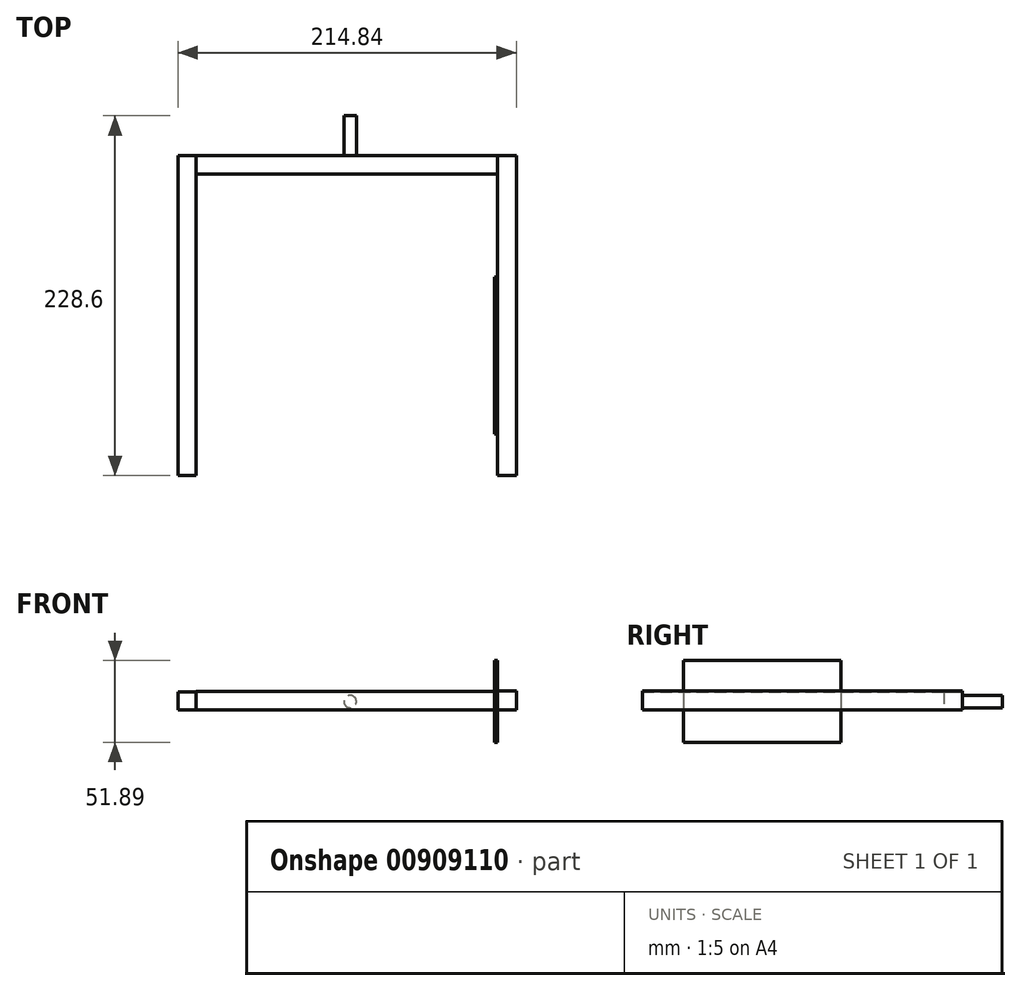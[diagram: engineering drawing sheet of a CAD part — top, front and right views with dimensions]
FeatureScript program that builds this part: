
annotation { "Feature Type Name" : "Feature", "Feature Type Description" : "" }
export const myFeature = defineFeature(function(context is Context, id is Id, definition is map)
    precondition{}
    {
        {
            var Q0;
            Q0=qCreatedBy(makeId("Front.planeOp"),FACE);
            var sketch = newSketch(context, id + "F0", { "sketchPlane" : qUnion([Q0])});
            skLineSegment(sketch, "E0.bottom", {"start": v(0, 0) * mm, "end": v(-11.43, 0) * mm});
            skLineSegment(sketch, "E0.top", {"start": v(0, 11.29) * mm, "end": v(-11.43, 11.29) * mm});
            skLineSegment(sketch, "E0.left", {"start": v(0, 0) * mm, "end": v(0, 11.29) * mm});
            skLineSegment(sketch, "E0.right", {"start": v(-11.43, 0) * mm, "end": v(-11.43, 11.29) * mm});
            skSolve(sketch);
        }
        {
            var Q0;
            Q0=makeQuery(id+"F0.imprint","IMPRINT",FACE,{"disambiguationData":[TD([[makeQuery(id+"F0.imprint","IMPRINT",EDGE,{"derivedFrom":sQuery(id+"F0.wireOp",EDGE,"E0.bottom")}),-1.0]])]});
            extrude(context, id + "F1", {"entities" : qUnion([Q0]), "depth" : 203.2 * mm, "offsetDistance" : 25.4 * mm});
        }
        {
            var Q0;
            Q0=qCreatedBy(makeId("Right.planeOp"),FACE);
            var sketch = newSketch(context, id + "F2", { "sketchPlane" : qUnion([Q0])});
            skLineSegment(sketch, "E1.bottom", {"start": v(0, 11.57) * mm, "end": v(-11.56, 11.57) * mm});
            skLineSegment(sketch, "E1.top", {"start": v(0, 0) * mm, "end": v(-11.56, 0) * mm});
            skLineSegment(sketch, "E1.left", {"start": v(0, 11.57) * mm, "end": v(0, 0) * mm});
            skLineSegment(sketch, "E1.right", {"start": v(-11.56, 11.57) * mm, "end": v(-11.56, 0) * mm});
            skSolve(sketch);
        }
        {
            var Q0;
            Q0=makeQuery(id+"F2.imprint","IMPRINT",FACE,{"disambiguationData":[TD([[makeQuery(id+"F2.imprint","IMPRINT",EDGE,{"derivedFrom":sQuery(id+"F2.wireOp",EDGE,"E1.bottom")}),1.0]])]});
            extrude(context, id + "F3", {"entities" : qUnion([Q0]), "operationType" : NewBodyOperationType.ADD, "depth" : 203.2 * mm, "offsetDistance" : 25.4 * mm});
        }
        {
            var Q0;
            Q0=qCreatedBy(makeId("Front.planeOp"),FACE);
            var sketch = newSketch(context, id + "F4", { "sketchPlane" : qUnion([Q0])});
            skLineSegment(sketch, "E2.bottom", {"start": v(203.4, 11.86) * mm, "end": v(191.54, 11.86) * mm});
            skLineSegment(sketch, "E2.top", {"start": v(203.4, 0) * mm, "end": v(191.54, 0) * mm});
            skLineSegment(sketch, "E2.left", {"start": v(203.4, 11.86) * mm, "end": v(203.4, 0) * mm});
            skLineSegment(sketch, "E2.right", {"start": v(191.54, 11.86) * mm, "end": v(191.54, 0) * mm});
            skSolve(sketch);
        }
        {
            var Q0;
            Q0 = qSketchRegion(id + "F4", true);
            extrude(context, id + "F5", {"entities" : qUnion([Q0]), "operationType" : NewBodyOperationType.ADD, "depth" : 203.2 * mm, "offsetDistance" : 25.4 * mm});
        }
        {
            var Q0;
            Q0=makeQuery(id+"F5.opExtrude","SWEPT_FACE",FACE,{"disambiguationData":[OSD([sQuery(id+"F4.wireOp",EDGE,"E2.right")])]});
            var sketch = newSketch(context, id + "F6", { "sketchPlane" : qUnion([Q0])});
            skLineSegment(sketch, "E3.bottom", {"start": v(77.07, 31.27) * mm, "end": v(176.89, 31.27) * mm});
            skLineSegment(sketch, "E3.top", {"start": v(77.07, -20.62) * mm, "end": v(176.89, -20.62) * mm});
            skLineSegment(sketch, "E3.left", {"start": v(77.07, 31.27) * mm, "end": v(77.07, -20.62) * mm});
            skLineSegment(sketch, "E3.right", {"start": v(176.89, 31.27) * mm, "end": v(176.89, -20.62) * mm});
            skSolve(sketch);
        }
        {
            var Q0;
            Q0 = qSketchRegion(id + "F6", true);
            extrude(context, id + "F7", {"entities" : qUnion([Q0]), "operationType" : NewBodyOperationType.ADD, "depth" : 2.03 * mm, "offsetDistance" : 25.4 * mm});
        }
        {
            var Q0;
            Q0=makeQuery(id+"F5.boolean.opBoolean","MERGE",FACE,{"derivedFrom":[makeQuery(id+"F3.boolean.opBoolean","MERGE",FACE,{"derivedFrom":[makeQuery(id+"F1.opExtrude","CAP_FACE",FACE,{"disambiguationData":[OSD([sQuery(id+"F0.wireOp",EDGE,"E0.bottom"),sQuery(id+"F0.wireOp",EDGE,"E0.top"),sQuery(id+"F0.wireOp",EDGE,"E0.left"),sQuery(id+"F0.wireOp",EDGE,"E0.right")])],"isStart":true}),makeQuery(id+"F3.opExtrude","SWEPT_FACE",FACE,{"disambiguationData":[OSD([sQuery(id+"F2.wireOp",EDGE,"E1.left")])]})]}),makeQuery(id+"F5.opExtrude","CAP_FACE",FACE,{"disambiguationData":[OSD([sQuery(id+"F4.wireOp",EDGE,"E2.bottom"),sQuery(id+"F4.wireOp",EDGE,"E2.top"),sQuery(id+"F4.wireOp",EDGE,"E2.left"),sQuery(id+"F4.wireOp",EDGE,"E2.right")])],"isStart":true})]});
            var sketch = newSketch(context, id + "F8", { "sketchPlane" : qUnion([Q0])});
            skCircle(sketch, "E4", {"center": v(-97.9, 5.2) * mm, "radius": 3.94 * mm});
            skSolve(sketch);
        }
        {
            var Q0;
            Q0 = qSketchRegion(id + "F8", true);
            var Q1;
            Q1=sQuery(id+"F8.wireOp",EDGE,"E4");
            extrude(context, id + "F9", {"entities" : qUnion([Q0]), "operationType" : NewBodyOperationType.ADD, "surfaceEntities" : qUnion([Q1]), "depth" : 25.4 * mm, "offsetDistance" : 25.4 * mm});
        }
    });
